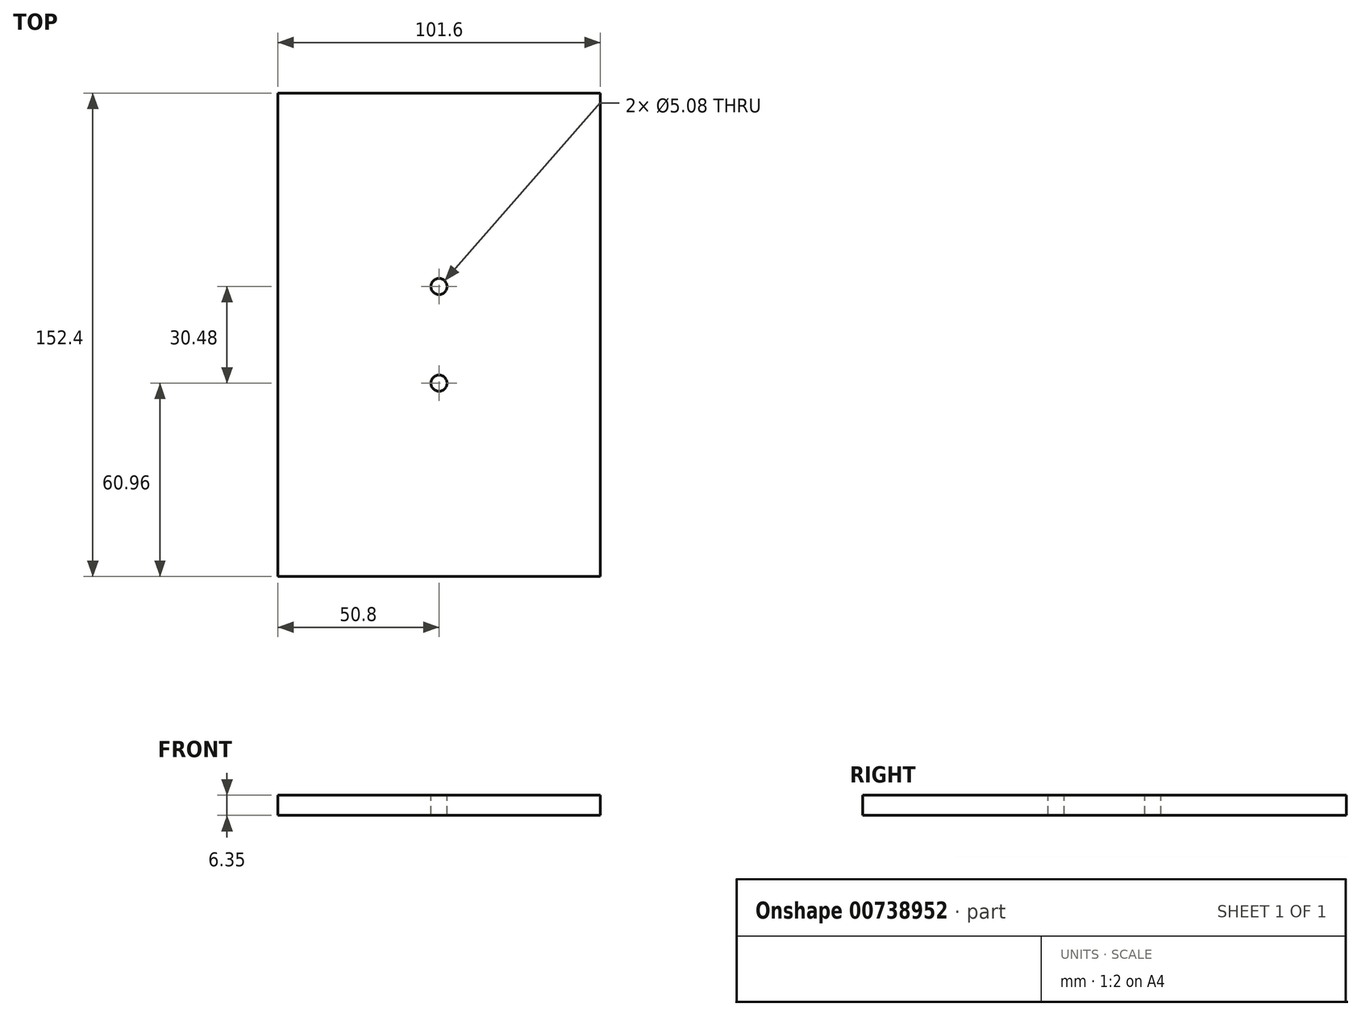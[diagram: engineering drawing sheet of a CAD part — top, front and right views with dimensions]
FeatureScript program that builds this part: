
annotation { "Feature Type Name" : "Feature", "Feature Type Description" : "" }
export const myFeature = defineFeature(function(context is Context, id is Id, definition is map)
    precondition{}
    {
        {
            var Q0;
            Q0=qCreatedBy(makeId("Top.planeOp"),FACE);
            var sketch = newSketch(context, id + "F0", { "sketchPlane" : qUnion([Q0])});
            skLineSegment(sketch, "E0.bottom", {"start": v(50.8, -76.2) * mm, "end": v(-50.8, -76.2) * mm});
            skLineSegment(sketch, "E0.top", {"start": v(50.8, 76.2) * mm, "end": v(-50.8, 76.2) * mm});
            skLineSegment(sketch, "E0.left", {"start": v(50.8, -76.2) * mm, "end": v(50.8, 76.2) * mm});
            skLineSegment(sketch, "E0.right", {"start": v(-50.8, -76.2) * mm, "end": v(-50.8, 76.2) * mm});
            skPoint(sketch, "E0.middle", {"position": v(0, 0) * mm});
            skSolve(sketch);
        }
        {
            var Q0;
            Q0=makeQuery(id+"F0.imprint","IMPRINT",FACE,{"disambiguationData":[TD([[makeQuery(id+"F0.imprint","IMPRINT",EDGE,{"derivedFrom":sQuery(id+"F0.wireOp",EDGE,"E0.bottom")}),-1.0]])]});
            extrude(context, id + "F1", {"entities" : qUnion([Q0]), "depth" : 6.35 * mm, "offsetDistance" : 25.4 * mm});
        }
        {
            var Q0;
            Q0=makeQuery(id+"F1.opExtrude","CAP_FACE",FACE,{"disambiguationData":[OSD([sQuery(id+"F0.wireOp",EDGE,"E0.bottom"),sQuery(id+"F0.wireOp",EDGE,"E0.top"),sQuery(id+"F0.wireOp",EDGE,"E0.left"),sQuery(id+"F0.wireOp",EDGE,"E0.right")])],"isStart":false});
            var sketch = newSketch(context, id + "F2", { "sketchPlane" : qUnion([Q0])});
            skLineSegment(sketch, "E1", {"start": v(0, 76.2) * mm, "end": v(0, -76.2) * mm});
            skPoint(sketch, "E2", {"position": v(0, 15.24) * mm});
            skLineSegment(sketch, "E3", {"start": v(0, 15.24) * mm, "end": v(0, 76.2) * mm});
            skPoint(sketch, "E4", {"position": v(0, -15.24) * mm});
            skLineSegment(sketch, "E5", {"start": v(0, -15.24) * mm, "end": v(0, -76.2) * mm});
            skSolve(sketch);
        }
        {
            var Q0;
            Q0=sQuery(id+"F2.wireOp",VERTEX,"E2");
            var Q1;
            Q1=sQuery(id+"F2.wireOp",VERTEX,"E4");
            var Q2;
            Q2=makeQuery(id+"F1.opExtrude","SWEPT_BODY",BODY,{"disambiguationData":[OSD([sQuery(id+"F0.wireOp",EDGE,"E0.bottom"),sQuery(id+"F0.wireOp",EDGE,"E0.top"),sQuery(id+"F0.wireOp",EDGE,"E0.left"),sQuery(id+"F0.wireOp",EDGE,"E0.right")])]});
            hole(context, id + "F3", {"style" : HoleStyle.SIMPLE, "endStyle" : HoleEndStyle.THROUGH, "holeDiameter" : 5.08 * mm, "majorDiameter" : 6.35 * mm, "isTappedThrough" : true, "tappedDepth" : 12.7 * mm, "tapClearance" : 3, "locations" : qUnion([Q0, Q1]), "scope" : qUnion([Q2])});
        }
    });
